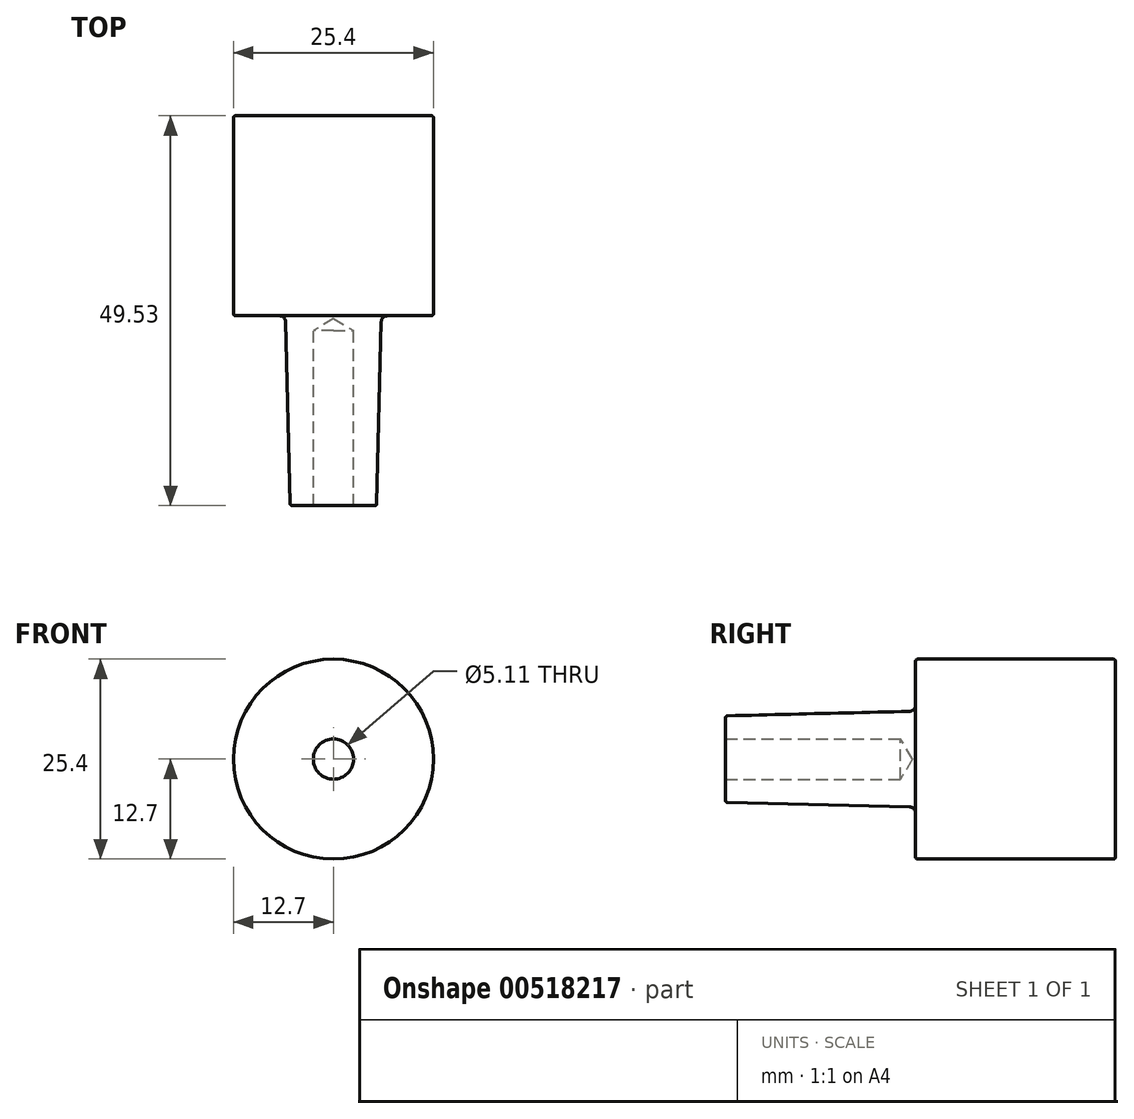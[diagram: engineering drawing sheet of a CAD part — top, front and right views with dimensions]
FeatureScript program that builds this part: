
annotation { "Feature Type Name" : "Feature", "Feature Type Description" : "" }
export const myFeature = defineFeature(function(context is Context, id is Id, definition is map)
    precondition{}
    {
        {
            var Q0;
            Q0=qCreatedBy(makeId("Right.planeOp"),FACE);
            var sketch = newSketch(context, id + "F0", { "sketchPlane" : qUnion([Q0])});
            skLineSegment(sketch, "E0", {"start": v(25.4, 0) * mm, "end": v(25.4, 12.7) * mm});
            skLineSegment(sketch, "E1", {"start": v(25.4, 12.7) * mm, "end": v(0, 12.7) * mm});
            skLineSegment(sketch, "E2", {"start": v(0, 12.7) * mm, "end": v(0, 6.1) * mm});
            skLineSegment(sketch, "E3", {"start": v(0, 6.1) * mm, "end": v(-24.13, 5.5) * mm});
            skLineSegment(sketch, "E4", {"start": v(-24.13, 5.5) * mm, "end": v(-24.13, 0) * mm});
            skLineSegment(sketch, "E5", {"start": v(-24.13, 0) * mm, "end": v(25.4, 0) * mm});
            skLineSegment(sketch, "E6", {"start": v(-59.9, 0) * mm, "end": v(67.6, 0) * mm, "construction": true});
            skSolve(sketch);
        }
        {
            var Q0;
            Q0 = qSketchRegion(id + "F0", true);
            var Q1;
            Q1=sQuery(id+"F0.wireOp",EDGE,"E5");
            revolve(context, id + "F1", {"entities" : qUnion([Q0]), "axis" : qUnion([Q1]), "revolveType" : RevolveType.FULL});
        }
        {
            var Q0;
            Q0=makeQuery(id+"F1.opRevolve","SWEPT_FACE",FACE,{"disambiguationData":[OSD([sQuery(id+"F0.wireOp",EDGE,"E4")])]});
            var sketch = newSketch(context, id + "F2", { "sketchPlane" : qUnion([Q0])});
            skPoint(sketch, "E7", {"position": v(0, 0) * mm});
            skSolve(sketch);
        }
        {
            var Q0;
            Q0=sQuery(id+"F2.wireOp",VERTEX,"E7");
            var Q1;
            Q1=makeQuery(id+"F1.opRevolve","SWEPT_BODY",BODY,{"disambiguationData":[OSD([sQuery(id+"F0.wireOp",EDGE,"E0"),sQuery(id+"F0.wireOp",EDGE,"E1"),sQuery(id+"F0.wireOp",EDGE,"E2"),sQuery(id+"F0.wireOp",EDGE,"E3"),sQuery(id+"F0.wireOp",EDGE,"E4"),sQuery(id+"F0.wireOp",EDGE,"E5")])]});
            hole(context, id + "F3", {"style" : HoleStyle.SIMPLE, "endStyle" : HoleEndStyle.BLIND, "standardTappedOrClearance" : lookupTablePath({ "standard" : "ANSI", "engagement" : "75%", "pitch" : "20 tpi", "size" : "1/4", "type" : "Tapped" }), "standardBlindInLast" : lookupTablePath({ "standard" : "ANSI", "engagement" : "75%", "pitch" : "20 tpi", "size" : "1/4", "type" : "Tapped" }), "holeDiameter" : 5.1 * mm, "showTappedDepth" : true, "holeDepth" : 22.22 * mm, "isTappedThrough" : true, "tappedDepth" : 18.41 * mm, "tapClearance" : 3, "startFromSketch" : true, "locations" : qUnion([Q0]), "scope" : qUnion([Q1]), "majorDiameter" : 6.35 * mm});
        }
        {
            var Q0;
            Q0=makeQuery(id+"F1.opRevolve","SWEPT_EDGE",EDGE,{"disambiguationData":[OSD([sQuery(id+"F0.wireOp",EDGE,"E2"),sQuery(id+"F0.wireOp",EDGE,"E3")])]});
            fillet(context, id + "F4", {"entities" : qUnion([Q0]), "radius" : 0.76 * mm, "tangentPropagation" : true, "allowEdgeOverflow" : false});
        }
        {
            var Q0;
            Q0=makeQuery(id+"F1.opRevolve","SWEPT_EDGE",EDGE,{"disambiguationData":[OSD([sQuery(id+"F0.wireOp",EDGE,"E1"),sQuery(id+"F0.wireOp",EDGE,"E2")])]});
            var Q1;
            Q1=makeQuery(id+"F1.opRevolve","SWEPT_EDGE",EDGE,{"disambiguationData":[OSD([sQuery(id+"F0.wireOp",EDGE,"E0"),sQuery(id+"F0.wireOp",EDGE,"E1")])]});
            var Q2;
            Q2=makeQuery(id+"F1.opRevolve","SWEPT_EDGE",EDGE,{"disambiguationData":[OSD([sQuery(id+"F0.wireOp",EDGE,"E3"),sQuery(id+"F0.wireOp",EDGE,"E4")])]});
            fillet(context, id + "F5", {"entities" : qUnion([Q0, Q1, Q2]), "radius" : 0.25 * mm, "tangentPropagation" : true, "allowEdgeOverflow" : false});
        }
    });
